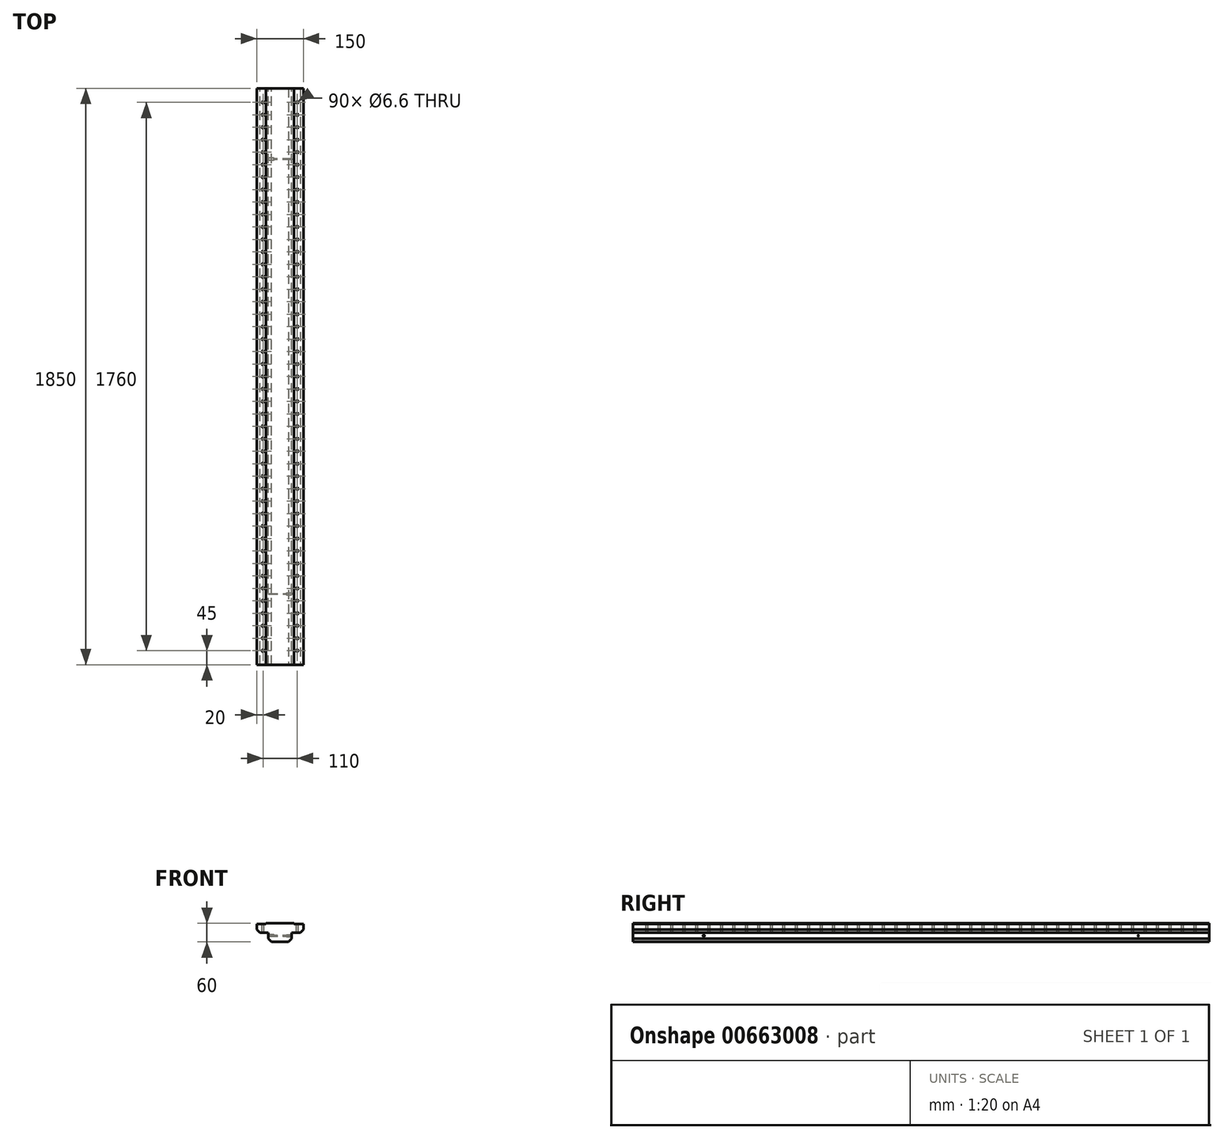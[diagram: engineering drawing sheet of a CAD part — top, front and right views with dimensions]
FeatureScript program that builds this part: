
annotation { "Feature Type Name" : "Feature", "Feature Type Description" : "" }
export const myFeature = defineFeature(function(context is Context, id is Id, definition is map)
    precondition{}
    {
        {
            var Q0;
            Q0=qCreatedBy(makeId("Front.planeOp"),FACE);
            var sketch = newSketch(context, id + "F0", { "sketchPlane" : qUnion([Q0])});
            skLineSegment(sketch, "E0", {"start": v(0, 0) * mm, "end": v(-75, 0) * mm});
            skLineSegment(sketch, "E1", {"start": v(-75, 0) * mm, "end": v(-75, -30) * mm});
            skLineSegment(sketch, "E2", {"start": v(-75, -30) * mm, "end": v(-37.5, -30) * mm});
            skLineSegment(sketch, "E3", {"start": v(-37.5, -30) * mm, "end": v(-37.5, -60) * mm});
            skLineSegment(sketch, "E4", {"start": v(-37.5, -60) * mm, "end": v(0, -60) * mm});
            skLineSegment(sketch, "E5", {"start": v(0, -60) * mm, "end": v(37.5, -60) * mm});
            skLineSegment(sketch, "E6", {"start": v(37.5, -60) * mm, "end": v(37.5, -30) * mm});
            skLineSegment(sketch, "E7", {"start": v(37.5, -30) * mm, "end": v(75, -30) * mm});
            skLineSegment(sketch, "E8", {"start": v(75, -30) * mm, "end": v(75, 0) * mm});
            skLineSegment(sketch, "E9", {"start": v(75, 0) * mm, "end": v(0, 0) * mm});
            skSolve(sketch);
        }
        {
            var Q0;
            Q0=makeQuery(id+"F0.imprint","IMPRINT",FACE,{"disambiguationData":[TD([[makeQuery(id+"F0.imprint","IMPRINT",EDGE,{"derivedFrom":sQuery(id+"F0.wireOp",EDGE,"E0")}),1.0]])]});
            extrude(context, id + "F1", {"entities" : qUnion([Q0]), "depth" : 1850 * mm, "offsetDistance" : 25 * mm});
        }
        {
            var Q0;
            Q0=makeQuery(id+"F1.opExtrude","SWEPT_EDGE",EDGE,{"disambiguationData":[OSD([sQuery(id+"F0.wireOp",EDGE,"E7"),sQuery(id+"F0.wireOp",EDGE,"E8")])]});
            var Q1;
            Q1=makeQuery(id+"F1.opExtrude","SWEPT_EDGE",EDGE,{"disambiguationData":[OSD([sQuery(id+"F0.wireOp",EDGE,"E1"),sQuery(id+"F0.wireOp",EDGE,"E2")])]});
            var Q2;
            Q2=makeQuery(id+"F1.opExtrude","SWEPT_EDGE",EDGE,{"disambiguationData":[OSD([sQuery(id+"F0.wireOp",EDGE,"E3"),sQuery(id+"F0.wireOp",EDGE,"E4")])]});
            var Q3;
            Q3=makeQuery(id+"F1.opExtrude","SWEPT_EDGE",EDGE,{"disambiguationData":[OSD([sQuery(id+"F0.wireOp",EDGE,"E5"),sQuery(id+"F0.wireOp",EDGE,"E6")])]});
            chamfer(context, id + "F2", {"entities" : qUnion([Q0, Q1, Q2, Q3]), "width" : 10 * mm, "tangentPropagation" : true});
        }
        {
            var Q0;
            Q0=makeQuery(id+"F1.opExtrude","SWEPT_FACE",FACE,{"disambiguationData":[OSD([sQuery(id+"F0.wireOp",EDGE,"E3")])]});
            var sketch = newSketch(context, id + "F3", { "sketchPlane" : qUnion([Q0])});
            skPoint(sketch, "E10", {"position": v(227.5, -40) * mm});
            skSolve(sketch);
        }
        {
            var Q0;
            Q0=sQuery(id+"F3.wireOp",VERTEX,"E10");
            var Q1;
            Q1=makeQuery(id+"F1.opExtrude","SWEPT_BODY",BODY,{"disambiguationData":[OSD([sQuery(id+"F0.wireOp",EDGE,"E0"),sQuery(id+"F0.wireOp",EDGE,"E1"),sQuery(id+"F0.wireOp",EDGE,"E2"),sQuery(id+"F0.wireOp",EDGE,"E3"),sQuery(id+"F0.wireOp",EDGE,"E4"),sQuery(id+"F0.wireOp",EDGE,"E5"),sQuery(id+"F0.wireOp",EDGE,"E6"),sQuery(id+"F0.wireOp",EDGE,"E7"),sQuery(id+"F0.wireOp",EDGE,"E8"),sQuery(id+"F0.wireOp",EDGE,"E9")])]});
            hole(context, id + "F4", {"style" : HoleStyle.SIMPLE, "endStyle" : HoleEndStyle.BLIND, "standardTappedOrClearance" : lookupTablePath({ "fit" : "Normal", "standard" : "ISO", "size" : "M6", "type" : "Clearance" }), "standardBlindInLast" : lookupTablePath({ "fit" : "Normal", "standard" : "ISO", "engagement" : "75%", "pitch" : "1 mm", "size" : "M6", "type" : "Clearance & tapped" }), "holeDiameter" : 6.6 * mm, "majorDiameter" : 5 * mm, "holeDepth" : 17.25 * mm, "isTappedThrough" : true, "tappedDepth" : 12 * mm, "tapClearance" : 3, "locations" : qUnion([Q0]), "scope" : qUnion([Q1])});
        }
        {
            var Q0;
            Q0=sQuery(id+"F3.wireOp",VERTEX,"E10");
            var Q1;
            Q1=makeQuery(id+"F1.opExtrude","SWEPT_BODY",BODY,{"disambiguationData":[OSD([sQuery(id+"F0.wireOp",EDGE,"E0"),sQuery(id+"F0.wireOp",EDGE,"E1"),sQuery(id+"F0.wireOp",EDGE,"E2"),sQuery(id+"F0.wireOp",EDGE,"E3"),sQuery(id+"F0.wireOp",EDGE,"E4"),sQuery(id+"F0.wireOp",EDGE,"E5"),sQuery(id+"F0.wireOp",EDGE,"E6"),sQuery(id+"F0.wireOp",EDGE,"E7"),sQuery(id+"F0.wireOp",EDGE,"E8"),sQuery(id+"F0.wireOp",EDGE,"E9")])]});
            hole(context, id + "F5", {"style" : HoleStyle.SIMPLE, "endStyle" : HoleEndStyle.THROUGH, "standardTappedOrClearance" : lookupTablePath({ "fit" : "Normal", "standard" : "ISO", "size" : "M2", "type" : "Clearance" }), "standardBlindInLast" : lookupTablePath({ "fit" : "Normal", "standard" : "ISO", "engagement" : "75%", "pitch" : "0.25 mm", "size" : "M2", "type" : "Clearance & tapped" }), "holeDiameter" : 2.4 * mm, "majorDiameter" : 5 * mm, "isTappedThrough" : true, "tappedDepth" : 12 * mm, "tapClearance" : 3, "locations" : qUnion([Q0]), "scope" : qUnion([Q1])});
        }
        {
            var Q0;
            Q0=makeQuery(id+"F1.opExtrude","SWEPT_FACE",FACE,{"disambiguationData":[OSD([sQuery(id+"F0.wireOp",EDGE,"E6")])]});
            var sketch = newSketch(context, id + "F6", { "sketchPlane" : qUnion([Q0])});
            skPoint(sketch, "E11", {"position": v(-1622.5, -40) * mm});
            skSolve(sketch);
        }
        {
            var Q0;
            Q0=sQuery(id+"F6.wireOp",VERTEX,"E11");
            var Q1;
            Q1=makeQuery(id+"F1.opExtrude","SWEPT_BODY",BODY,{"disambiguationData":[OSD([sQuery(id+"F0.wireOp",EDGE,"E0"),sQuery(id+"F0.wireOp",EDGE,"E1"),sQuery(id+"F0.wireOp",EDGE,"E2"),sQuery(id+"F0.wireOp",EDGE,"E3"),sQuery(id+"F0.wireOp",EDGE,"E4"),sQuery(id+"F0.wireOp",EDGE,"E5"),sQuery(id+"F0.wireOp",EDGE,"E6"),sQuery(id+"F0.wireOp",EDGE,"E7"),sQuery(id+"F0.wireOp",EDGE,"E8"),sQuery(id+"F0.wireOp",EDGE,"E9")])]});
            hole(context, id + "F7", {"style" : HoleStyle.SIMPLE, "endStyle" : HoleEndStyle.BLIND, "standardTappedOrClearance" : lookupTablePath({ "fit" : "Normal", "standard" : "ISO", "size" : "M5", "type" : "Clearance" }), "standardBlindInLast" : lookupTablePath({ "fit" : "Normal", "standard" : "ISO", "engagement" : "75%", "pitch" : "0.8 mm", "size" : "M5", "type" : "Clearance & tapped" }), "holeDiameter" : 5.5 * mm, "majorDiameter" : 5 * mm, "holeDepth" : 17.25 * mm, "isTappedThrough" : true, "tappedDepth" : 12 * mm, "tapClearance" : 3, "locations" : qUnion([Q0]), "scope" : qUnion([Q1])});
        }
        {
            var Q0;
            Q0=sQuery(id+"F6.wireOp",VERTEX,"E11");
            var Q1;
            Q1=makeQuery(id+"F1.opExtrude","SWEPT_BODY",BODY,{"disambiguationData":[OSD([sQuery(id+"F0.wireOp",EDGE,"E0"),sQuery(id+"F0.wireOp",EDGE,"E1"),sQuery(id+"F0.wireOp",EDGE,"E2"),sQuery(id+"F0.wireOp",EDGE,"E3"),sQuery(id+"F0.wireOp",EDGE,"E4"),sQuery(id+"F0.wireOp",EDGE,"E5"),sQuery(id+"F0.wireOp",EDGE,"E6"),sQuery(id+"F0.wireOp",EDGE,"E7"),sQuery(id+"F0.wireOp",EDGE,"E8"),sQuery(id+"F0.wireOp",EDGE,"E9")])]});
            hole(context, id + "F8", {"style" : HoleStyle.SIMPLE, "endStyle" : HoleEndStyle.THROUGH, "standardTappedOrClearance" : lookupTablePath({ "fit" : "Normal", "standard" : "ISO", "size" : "M2", "type" : "Clearance" }), "standardBlindInLast" : lookupTablePath({ "fit" : "Normal", "standard" : "ISO", "engagement" : "75%", "pitch" : "0.25 mm", "size" : "M2", "type" : "Clearance & tapped" }), "holeDiameter" : 2.4 * mm, "majorDiameter" : 5 * mm, "isTappedThrough" : true, "tappedDepth" : 12 * mm, "tapClearance" : 3, "locations" : qUnion([Q0]), "scope" : qUnion([Q1])});
        }
        {
            var Q0;
            Q0=makeQuery(id+"F1.opExtrude","CAP_FACE",FACE,{"disambiguationData":[OSD([sQuery(id+"F0.wireOp",EDGE,"E0"),sQuery(id+"F0.wireOp",EDGE,"E1"),sQuery(id+"F0.wireOp",EDGE,"E2"),sQuery(id+"F0.wireOp",EDGE,"E3"),sQuery(id+"F0.wireOp",EDGE,"E4"),sQuery(id+"F0.wireOp",EDGE,"E5"),sQuery(id+"F0.wireOp",EDGE,"E6"),sQuery(id+"F0.wireOp",EDGE,"E7"),sQuery(id+"F0.wireOp",EDGE,"E8"),sQuery(id+"F0.wireOp",EDGE,"E9")])],"isStart":false});
            var sketch = newSketch(context, id + "F9", { "sketchPlane" : qUnion([Q0])});
            skLineSegment(sketch, "E12", {"start": v(-75, -3) * mm, "end": v(-45, -3) * mm});
            skLineSegment(sketch, "E13", {"start": v(-45, -3) * mm, "end": v(-45, 0) * mm});
            skLineSegment(sketch, "E14", {"start": v(75, -3) * mm, "end": v(45, -3) * mm});
            skLineSegment(sketch, "E15", {"start": v(45, -3) * mm, "end": v(45, 0) * mm});
            skSolve(sketch);
        }
        {
            var Q0;
            {var subQ0=sQuery(id+"F9.wireOp",EDGE,"E12");Q0=makeQuery(id+"F9.imprint","IMPRINT",FACE,{"disambiguationData":[TD([[makeQuery(id+"F9.imprint","IMPRINT",EDGE,{"derivedFrom":subQ0}),1.0]])]});}
            var Q1;
            {var subQ0=sQuery(id+"F9.wireOp",EDGE,"E14");Q1=makeQuery(id+"F9.imprint","IMPRINT",FACE,{"disambiguationData":[TD([[makeQuery(id+"F9.imprint","IMPRINT",EDGE,{"derivedFrom":subQ0}),-1.0]])]});}
            extrude(context, id + "F10", {"entities" : qUnion([Q0, Q1]), "operationType" : NewBodyOperationType.REMOVE, "endBound" : BoundingType.THROUGH_ALL, "oppositeDirection" : true, "depth" : 25 * mm, "offsetDistance" : 25 * mm});
        }
        {
            var Q0;
            Q0=makeQuery(id+"F10.boolean.opBoolean","COPY",FACE,{"derivedFrom":makeQuery(id+"F10.opExtrude","SWEPT_FACE",FACE,{"disambiguationData":[OSD([sQuery(id+"F9.wireOp",EDGE,"E12")])]})});
            var sketch = newSketch(context, id + "F11", { "sketchPlane" : qUnion([Q0])});
            skPoint(sketch, "E16", {"position": v(-55, -1805) * mm});
            skPoint(sketch, "E16.positionSnap0", {"position": v(-60, -1850) * mm});
            skPoint(sketch, "E17.0.1.0", {"position": v(-55, -1765) * mm});
            skPoint(sketch, "E17.0.2.0", {"position": v(-55, -1725) * mm});
            skPoint(sketch, "E17.0.3.0", {"position": v(-55, -1685) * mm});
            skPoint(sketch, "E17.0.4.0", {"position": v(-55, -1645) * mm});
            skPoint(sketch, "E17.0.5.0", {"position": v(-55, -1605) * mm});
            skPoint(sketch, "E17.0.6.0", {"position": v(-55, -1565) * mm});
            skPoint(sketch, "E17.0.7.0", {"position": v(-55, -1525) * mm});
            skPoint(sketch, "E17.0.8.0", {"position": v(-55, -1485) * mm});
            skPoint(sketch, "E17.0.9.0", {"position": v(-55, -1445) * mm});
            skPoint(sketch, "E17.0.10.0", {"position": v(-55, -1405) * mm});
            skPoint(sketch, "E17.0.11.0", {"position": v(-55, -1365) * mm});
            skPoint(sketch, "E17.0.12.0", {"position": v(-55, -1325) * mm});
            skPoint(sketch, "E17.0.13.0", {"position": v(-55, -1285) * mm});
            skPoint(sketch, "E17.0.14.0", {"position": v(-55, -1245) * mm});
            skPoint(sketch, "E17.0.15.0", {"position": v(-55, -1205) * mm});
            skPoint(sketch, "E17.0.16.0", {"position": v(-55, -1165) * mm});
            skPoint(sketch, "E17.0.17.0", {"position": v(-55, -1125) * mm});
            skPoint(sketch, "E17.0.18.0", {"position": v(-55, -1085) * mm});
            skPoint(sketch, "E17.0.19.0", {"position": v(-55, -1045) * mm});
            skPoint(sketch, "E17.0.20.0", {"position": v(-55, -1005) * mm});
            skPoint(sketch, "E17.0.21.0", {"position": v(-55, -965) * mm});
            skPoint(sketch, "E17.0.22.0", {"position": v(-55, -925) * mm});
            skPoint(sketch, "E17.0.23.0", {"position": v(-55, -885) * mm});
            skPoint(sketch, "E17.0.24.0", {"position": v(-55, -845) * mm});
            skPoint(sketch, "E17.0.25.0", {"position": v(-55, -805) * mm});
            skPoint(sketch, "E17.0.26.0", {"position": v(-55, -765) * mm});
            skPoint(sketch, "E17.0.27.0", {"position": v(-55, -725) * mm});
            skPoint(sketch, "E17.0.28.0", {"position": v(-55, -685) * mm});
            skPoint(sketch, "E17.0.29.0", {"position": v(-55, -645) * mm});
            skPoint(sketch, "E17.0.30.0", {"position": v(-55, -605) * mm});
            skPoint(sketch, "E17.0.31.0", {"position": v(-55, -565) * mm});
            skPoint(sketch, "E17.0.32.0", {"position": v(-55, -525) * mm});
            skPoint(sketch, "E17.0.33.0", {"position": v(-55, -485) * mm});
            skPoint(sketch, "E17.0.34.0", {"position": v(-55, -445) * mm});
            skPoint(sketch, "E17.0.35.0", {"position": v(-55, -405) * mm});
            skPoint(sketch, "E17.0.36.0", {"position": v(-55, -365) * mm});
            skPoint(sketch, "E17.0.37.0", {"position": v(-55, -325) * mm});
            skPoint(sketch, "E17.0.38.0", {"position": v(-55, -285) * mm});
            skPoint(sketch, "E17.0.39.0", {"position": v(-55, -245) * mm});
            skPoint(sketch, "E17.0.40.0", {"position": v(-55, -205) * mm});
            skPoint(sketch, "E17.0.41.0", {"position": v(-55, -165) * mm});
            skPoint(sketch, "E17.0.42.0", {"position": v(-55, -125) * mm});
            skPoint(sketch, "E17.0.43.0", {"position": v(-55, -85) * mm});
            skPoint(sketch, "E17.0.44.0", {"position": v(-55, -45) * mm});
            skLineSegment(sketch, "E17.direction1", {"start": v(-55, -1805) * mm, "end": v(-30, -1805) * mm, "construction": true});
            skLineSegment(sketch, "E17.direction2", {"start": v(-55, -1805) * mm, "end": v(-55, -1765) * mm, "construction": true});
            skSolve(sketch);
        }
        {
            var Q0;
            Q0=sQuery(id+"F11.wireOp",VERTEX,"E17.0.44.0");
            var Q1;
            Q1=sQuery(id+"F11.wireOp",VERTEX,"E17.0.43.0");
            var Q2;
            Q2=sQuery(id+"F11.wireOp",VERTEX,"E17.0.42.0");
            var Q3;
            Q3=sQuery(id+"F11.wireOp",VERTEX,"E17.0.41.0");
            var Q4;
            Q4=sQuery(id+"F11.wireOp",VERTEX,"E17.0.40.0");
            var Q5;
            Q5=sQuery(id+"F11.wireOp",VERTEX,"E17.0.39.0");
            var Q6;
            Q6=sQuery(id+"F11.wireOp",VERTEX,"E17.0.38.0");
            var Q7;
            Q7=sQuery(id+"F11.wireOp",VERTEX,"E17.0.37.0");
            var Q8;
            Q8=sQuery(id+"F11.wireOp",VERTEX,"E17.0.36.0");
            var Q9;
            Q9=sQuery(id+"F11.wireOp",VERTEX,"E17.0.35.0");
            var Q10;
            Q10=sQuery(id+"F11.wireOp",VERTEX,"E17.0.34.0");
            var Q11;
            Q11=sQuery(id+"F11.wireOp",VERTEX,"E17.0.33.0");
            var Q12;
            Q12=sQuery(id+"F11.wireOp",VERTEX,"E17.0.32.0");
            var Q13;
            Q13=sQuery(id+"F11.wireOp",VERTEX,"E17.0.31.0");
            var Q14;
            Q14=sQuery(id+"F11.wireOp",VERTEX,"E17.0.30.0");
            var Q15;
            Q15=sQuery(id+"F11.wireOp",VERTEX,"E17.0.29.0");
            var Q16;
            Q16=sQuery(id+"F11.wireOp",VERTEX,"E17.0.28.0");
            var Q17;
            Q17=sQuery(id+"F11.wireOp",VERTEX,"E17.0.27.0");
            var Q18;
            Q18=sQuery(id+"F11.wireOp",VERTEX,"E17.0.26.0");
            var Q19;
            Q19=sQuery(id+"F11.wireOp",VERTEX,"E17.0.25.0");
            var Q20;
            Q20=sQuery(id+"F11.wireOp",VERTEX,"E17.0.24.0");
            var Q21;
            Q21=sQuery(id+"F11.wireOp",VERTEX,"E17.0.23.0");
            var Q22;
            Q22=sQuery(id+"F11.wireOp",VERTEX,"E17.0.22.0");
            var Q23;
            Q23=sQuery(id+"F11.wireOp",VERTEX,"E17.0.21.0");
            var Q24;
            Q24=sQuery(id+"F11.wireOp",VERTEX,"E17.0.20.0");
            var Q25;
            Q25=sQuery(id+"F11.wireOp",VERTEX,"E17.0.19.0");
            var Q26;
            Q26=sQuery(id+"F11.wireOp",VERTEX,"E17.0.18.0");
            var Q27;
            Q27=sQuery(id+"F11.wireOp",VERTEX,"E17.0.17.0");
            var Q28;
            Q28=sQuery(id+"F11.wireOp",VERTEX,"E17.0.16.0");
            var Q29;
            Q29=sQuery(id+"F11.wireOp",VERTEX,"E17.0.15.0");
            var Q30;
            Q30=sQuery(id+"F11.wireOp",VERTEX,"E17.0.14.0");
            var Q31;
            Q31=sQuery(id+"F11.wireOp",VERTEX,"E17.0.13.0");
            var Q32;
            Q32=sQuery(id+"F11.wireOp",VERTEX,"E17.0.12.0");
            var Q33;
            Q33=sQuery(id+"F11.wireOp",VERTEX,"E17.0.11.0");
            var Q34;
            Q34=sQuery(id+"F11.wireOp",VERTEX,"E17.0.10.0");
            var Q35;
            Q35=sQuery(id+"F11.wireOp",VERTEX,"E17.0.9.0");
            var Q36;
            Q36=sQuery(id+"F11.wireOp",VERTEX,"E17.0.8.0");
            var Q37;
            Q37=sQuery(id+"F11.wireOp",VERTEX,"E17.0.7.0");
            var Q38;
            Q38=sQuery(id+"F11.wireOp",VERTEX,"E17.0.6.0");
            var Q39;
            Q39=sQuery(id+"F11.wireOp",VERTEX,"E17.0.5.0");
            var Q40;
            Q40=sQuery(id+"F11.wireOp",VERTEX,"E17.0.4.0");
            var Q41;
            Q41=sQuery(id+"F11.wireOp",VERTEX,"E17.0.3.0");
            var Q42;
            Q42=sQuery(id+"F11.wireOp",VERTEX,"E17.0.2.0");
            var Q43;
            Q43=sQuery(id+"F11.wireOp",VERTEX,"E17.direction2.end");
            var Q44;
            Q44=sQuery(id+"F11.wireOp",VERTEX,"E16");
            var Q45;
            Q45=makeQuery(id+"F1.opExtrude","SWEPT_BODY",BODY,{"disambiguationData":[OSD([sQuery(id+"F0.wireOp",EDGE,"E0"),sQuery(id+"F0.wireOp",EDGE,"E1"),sQuery(id+"F0.wireOp",EDGE,"E2"),sQuery(id+"F0.wireOp",EDGE,"E3"),sQuery(id+"F0.wireOp",EDGE,"E4"),sQuery(id+"F0.wireOp",EDGE,"E5"),sQuery(id+"F0.wireOp",EDGE,"E6"),sQuery(id+"F0.wireOp",EDGE,"E7"),sQuery(id+"F0.wireOp",EDGE,"E8"),sQuery(id+"F0.wireOp",EDGE,"E9")])]});
            hole(context, id + "F12", {"style" : HoleStyle.SIMPLE, "endStyle" : HoleEndStyle.THROUGH, "standardTappedOrClearance" : lookupTablePath({ "fit" : "Normal", "standard" : "ISO", "size" : "M6", "type" : "Clearance" }), "standardBlindInLast" : lookupTablePath({ "fit" : "Normal", "standard" : "ISO", "engagement" : "75%", "pitch" : "1 mm", "size" : "M6", "type" : "Clearance & tapped" }), "holeDiameter" : 6.6 * mm, "majorDiameter" : 5 * mm, "isTappedThrough" : true, "tappedDepth" : 12 * mm, "tapClearance" : 3, "locations" : qUnion([Q0, Q1, Q2, Q3, Q4, Q5, Q6, Q7, Q8, Q9, Q10, Q11, Q12, Q13, Q14, Q15, Q16, Q17, Q18, Q19, Q20, Q21, Q22, Q23, Q24, Q25, Q26, Q27, Q28, Q29, Q30, Q31, Q32, Q33, Q34, Q35, Q36, Q37, Q38, Q39, Q40, Q41, Q42, Q43, Q44]), "scope" : qUnion([Q45])});
        }
        {
            var Q0;
            Q0=makeQuery(id+"F10.boolean.opBoolean","COPY",FACE,{"derivedFrom":makeQuery(id+"F10.opExtrude","SWEPT_FACE",FACE,{"disambiguationData":[OSD([sQuery(id+"F9.wireOp",EDGE,"E14")])]})});
            var sketch = newSketch(context, id + "F13", { "sketchPlane" : qUnion([Q0])});
            skPoint(sketch, "E18", {"position": v(55, -1805) * mm});
            skPoint(sketch, "E19.0.1.0", {"position": v(55, -1765) * mm});
            skPoint(sketch, "E19.0.2.0", {"position": v(55, -1725) * mm});
            skPoint(sketch, "E19.0.3.0", {"position": v(55, -1685) * mm});
            skPoint(sketch, "E19.0.4.0", {"position": v(55, -1645) * mm});
            skPoint(sketch, "E19.0.5.0", {"position": v(55, -1605) * mm});
            skPoint(sketch, "E19.0.6.0", {"position": v(55, -1565) * mm});
            skPoint(sketch, "E19.0.7.0", {"position": v(55, -1525) * mm});
            skPoint(sketch, "E19.0.8.0", {"position": v(55, -1485) * mm});
            skPoint(sketch, "E19.0.9.0", {"position": v(55, -1445) * mm});
            skPoint(sketch, "E19.0.10.0", {"position": v(55, -1405) * mm});
            skPoint(sketch, "E19.0.11.0", {"position": v(55, -1365) * mm});
            skPoint(sketch, "E19.0.12.0", {"position": v(55, -1325) * mm});
            skPoint(sketch, "E19.0.13.0", {"position": v(55, -1285) * mm});
            skPoint(sketch, "E19.0.14.0", {"position": v(55, -1245) * mm});
            skPoint(sketch, "E19.0.15.0", {"position": v(55, -1205) * mm});
            skPoint(sketch, "E19.0.16.0", {"position": v(55, -1165) * mm});
            skPoint(sketch, "E19.0.17.0", {"position": v(55, -1125) * mm});
            skPoint(sketch, "E19.0.18.0", {"position": v(55, -1085) * mm});
            skPoint(sketch, "E19.0.19.0", {"position": v(55, -1045) * mm});
            skPoint(sketch, "E19.0.20.0", {"position": v(55, -1005) * mm});
            skPoint(sketch, "E19.0.21.0", {"position": v(55, -965) * mm});
            skPoint(sketch, "E19.0.22.0", {"position": v(55, -925) * mm});
            skPoint(sketch, "E19.0.23.0", {"position": v(55, -885) * mm});
            skPoint(sketch, "E19.0.24.0", {"position": v(55, -845) * mm});
            skPoint(sketch, "E19.0.25.0", {"position": v(55, -805) * mm});
            skPoint(sketch, "E19.0.26.0", {"position": v(55, -765) * mm});
            skPoint(sketch, "E19.0.27.0", {"position": v(55, -725) * mm});
            skPoint(sketch, "E19.0.28.0", {"position": v(55, -685) * mm});
            skPoint(sketch, "E19.0.29.0", {"position": v(55, -645) * mm});
            skPoint(sketch, "E19.0.30.0", {"position": v(55, -605) * mm});
            skPoint(sketch, "E19.0.31.0", {"position": v(55, -565) * mm});
            skPoint(sketch, "E19.0.32.0", {"position": v(55, -525) * mm});
            skPoint(sketch, "E19.0.33.0", {"position": v(55, -485) * mm});
            skPoint(sketch, "E19.0.34.0", {"position": v(55, -445) * mm});
            skPoint(sketch, "E19.0.35.0", {"position": v(55, -405) * mm});
            skPoint(sketch, "E19.0.36.0", {"position": v(55, -365) * mm});
            skPoint(sketch, "E19.0.37.0", {"position": v(55, -325) * mm});
            skPoint(sketch, "E19.0.38.0", {"position": v(55, -285) * mm});
            skPoint(sketch, "E19.0.39.0", {"position": v(55, -245) * mm});
            skPoint(sketch, "E19.0.40.0", {"position": v(55, -205) * mm});
            skPoint(sketch, "E19.0.41.0", {"position": v(55, -165) * mm});
            skPoint(sketch, "E19.0.42.0", {"position": v(55, -125) * mm});
            skPoint(sketch, "E19.0.43.0", {"position": v(55, -85) * mm});
            skPoint(sketch, "E19.0.44.0", {"position": v(55, -45) * mm});
            skLineSegment(sketch, "E19.direction1", {"start": v(55, -1805) * mm, "end": v(80, -1805) * mm, "construction": true});
            skLineSegment(sketch, "E19.direction2", {"start": v(55, -1805) * mm, "end": v(55, -1765) * mm, "construction": true});
            skSolve(sketch);
        }
        {
            var Q0;
            Q0=sQuery(id+"F13.wireOp",VERTEX,"E19.0.44.0");
            var Q1;
            Q1=sQuery(id+"F13.wireOp",VERTEX,"E19.0.43.0");
            var Q2;
            Q2=sQuery(id+"F13.wireOp",VERTEX,"E19.0.42.0");
            var Q3;
            Q3=sQuery(id+"F13.wireOp",VERTEX,"E19.0.41.0");
            var Q4;
            Q4=sQuery(id+"F13.wireOp",VERTEX,"E19.0.40.0");
            var Q5;
            Q5=sQuery(id+"F13.wireOp",VERTEX,"E19.0.39.0");
            var Q6;
            Q6=sQuery(id+"F13.wireOp",VERTEX,"E19.0.38.0");
            var Q7;
            Q7=sQuery(id+"F13.wireOp",VERTEX,"E19.0.37.0");
            var Q8;
            Q8=sQuery(id+"F13.wireOp",VERTEX,"E19.0.36.0");
            var Q9;
            Q9=sQuery(id+"F13.wireOp",VERTEX,"E19.0.35.0");
            var Q10;
            Q10=sQuery(id+"F13.wireOp",VERTEX,"E19.0.34.0");
            var Q11;
            Q11=sQuery(id+"F13.wireOp",VERTEX,"E19.0.33.0");
            var Q12;
            Q12=sQuery(id+"F13.wireOp",VERTEX,"E19.0.32.0");
            var Q13;
            Q13=sQuery(id+"F13.wireOp",VERTEX,"E19.0.31.0");
            var Q14;
            Q14=sQuery(id+"F13.wireOp",VERTEX,"E19.0.30.0");
            var Q15;
            Q15=sQuery(id+"F13.wireOp",VERTEX,"E19.0.29.0");
            var Q16;
            Q16=sQuery(id+"F13.wireOp",VERTEX,"E19.0.28.0");
            var Q17;
            Q17=sQuery(id+"F13.wireOp",VERTEX,"E19.0.27.0");
            var Q18;
            Q18=sQuery(id+"F13.wireOp",VERTEX,"E19.0.26.0");
            var Q19;
            Q19=sQuery(id+"F13.wireOp",VERTEX,"E19.0.25.0");
            var Q20;
            Q20=sQuery(id+"F13.wireOp",VERTEX,"E19.0.24.0");
            var Q21;
            Q21=sQuery(id+"F13.wireOp",VERTEX,"E19.0.23.0");
            var Q22;
            Q22=sQuery(id+"F13.wireOp",VERTEX,"E19.0.22.0");
            var Q23;
            Q23=sQuery(id+"F13.wireOp",VERTEX,"E19.0.21.0");
            var Q24;
            Q24=sQuery(id+"F13.wireOp",VERTEX,"E19.0.20.0");
            var Q25;
            Q25=sQuery(id+"F13.wireOp",VERTEX,"E19.0.19.0");
            var Q26;
            Q26=sQuery(id+"F13.wireOp",VERTEX,"E19.0.18.0");
            var Q27;
            Q27=sQuery(id+"F13.wireOp",VERTEX,"E19.0.17.0");
            var Q28;
            Q28=sQuery(id+"F13.wireOp",VERTEX,"E19.0.16.0");
            var Q29;
            Q29=sQuery(id+"F13.wireOp",VERTEX,"E19.0.15.0");
            var Q30;
            Q30=sQuery(id+"F13.wireOp",VERTEX,"E19.0.14.0");
            var Q31;
            Q31=sQuery(id+"F13.wireOp",VERTEX,"E19.0.13.0");
            var Q32;
            Q32=sQuery(id+"F13.wireOp",VERTEX,"E19.0.12.0");
            var Q33;
            Q33=sQuery(id+"F13.wireOp",VERTEX,"E19.0.11.0");
            var Q34;
            Q34=sQuery(id+"F13.wireOp",VERTEX,"E19.0.10.0");
            var Q35;
            Q35=sQuery(id+"F13.wireOp",VERTEX,"E19.0.9.0");
            var Q36;
            Q36=sQuery(id+"F13.wireOp",VERTEX,"E19.0.8.0");
            var Q37;
            Q37=sQuery(id+"F13.wireOp",VERTEX,"E19.0.7.0");
            var Q38;
            Q38=sQuery(id+"F13.wireOp",VERTEX,"E19.0.6.0");
            var Q39;
            Q39=sQuery(id+"F13.wireOp",VERTEX,"E19.0.5.0");
            var Q40;
            Q40=sQuery(id+"F13.wireOp",VERTEX,"E19.0.4.0");
            var Q41;
            Q41=sQuery(id+"F13.wireOp",VERTEX,"E19.0.3.0");
            var Q42;
            Q42=sQuery(id+"F13.wireOp",VERTEX,"E19.0.2.0");
            var Q43;
            Q43=sQuery(id+"F13.wireOp",VERTEX,"E19.0.1.0");
            var Q44;
            Q44=sQuery(id+"F13.wireOp",VERTEX,"E18");
            var Q45;
            Q45=makeQuery(id+"F1.opExtrude","SWEPT_BODY",BODY,{"disambiguationData":[OSD([sQuery(id+"F0.wireOp",EDGE,"E0"),sQuery(id+"F0.wireOp",EDGE,"E1"),sQuery(id+"F0.wireOp",EDGE,"E2"),sQuery(id+"F0.wireOp",EDGE,"E3"),sQuery(id+"F0.wireOp",EDGE,"E4"),sQuery(id+"F0.wireOp",EDGE,"E5"),sQuery(id+"F0.wireOp",EDGE,"E6"),sQuery(id+"F0.wireOp",EDGE,"E7"),sQuery(id+"F0.wireOp",EDGE,"E8"),sQuery(id+"F0.wireOp",EDGE,"E9")])]});
            hole(context, id + "F14", {"style" : HoleStyle.SIMPLE, "endStyle" : HoleEndStyle.THROUGH, "standardTappedOrClearance" : lookupTablePath({ "fit" : "Normal", "standard" : "ISO", "size" : "M6", "type" : "Clearance" }), "standardBlindInLast" : lookupTablePath({ "fit" : "Normal", "standard" : "ISO", "engagement" : "75%", "pitch" : "1 mm", "size" : "M6", "type" : "Clearance & tapped" }), "holeDiameter" : 6.6 * mm, "majorDiameter" : 5 * mm, "isTappedThrough" : true, "tappedDepth" : 12 * mm, "tapClearance" : 3, "locations" : qUnion([Q0, Q1, Q2, Q3, Q4, Q5, Q6, Q7, Q8, Q9, Q10, Q11, Q12, Q13, Q14, Q15, Q16, Q17, Q18, Q19, Q20, Q21, Q22, Q23, Q24, Q25, Q26, Q27, Q28, Q29, Q30, Q31, Q32, Q33, Q34, Q35, Q36, Q37, Q38, Q39, Q40, Q41, Q42, Q43, Q44]), "scope" : qUnion([Q45])});
        }
    });
